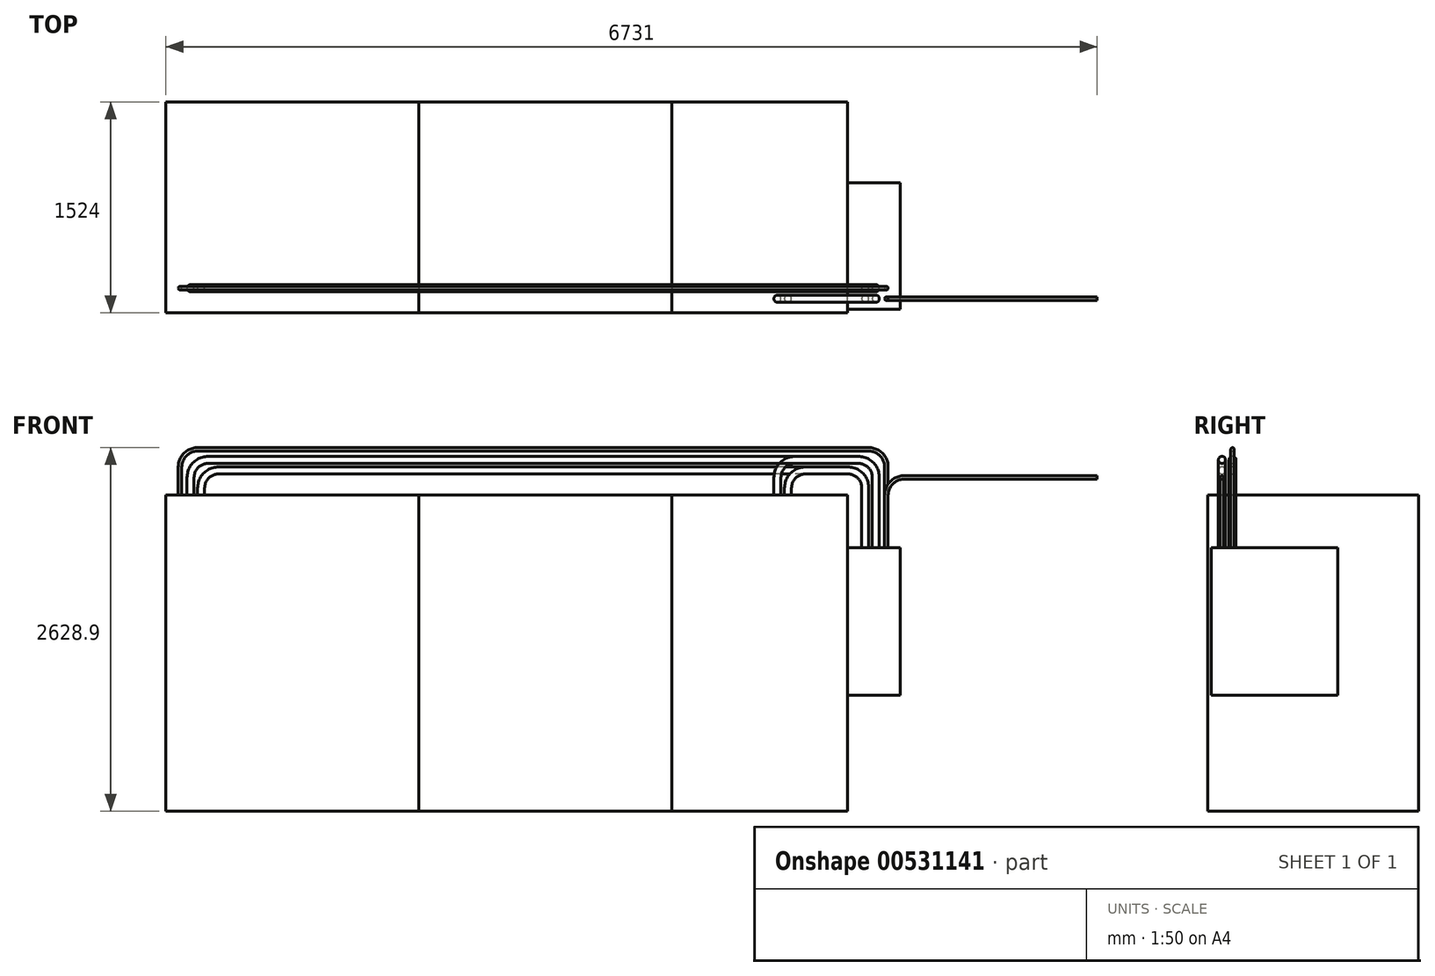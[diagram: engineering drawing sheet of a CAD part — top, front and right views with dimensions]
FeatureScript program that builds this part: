
annotation { "Feature Type Name" : "Feature", "Feature Type Description" : "" }
export const myFeature = defineFeature(function(context is Context, id is Id, definition is map)
    precondition{}
    {
        {
            var Q0;
            Q0=qCreatedBy(makeId("Top.planeOp"),FACE);
            var sketch = newSketch(context, id + "F0", { "sketchPlane" : qUnion([Q0])});
            skLineSegment(sketch, "E0.bottom", {"start": v(1828.8, 1524) * mm, "end": v(0, 1524) * mm});
            skLineSegment(sketch, "E0.top", {"start": v(1828.8, 0) * mm, "end": v(0, 0) * mm});
            skLineSegment(sketch, "E0.left", {"start": v(1828.8, 1524) * mm, "end": v(1828.8, 0) * mm});
            skLineSegment(sketch, "E0.right", {"start": v(0, 1524) * mm, "end": v(0, 0) * mm});
            skPoint(sketch, "E1.firstSnap0", {"position": v(0, 762) * mm});
            skPoint(sketch, "E2", {"position": v(0, 0) * mm});
            skSolve(sketch);
        }
        {
            var Q0;
            Q0=qCreatedBy(makeId("Top.planeOp"),FACE);
            var sketch = newSketch(context, id + "F1", { "sketchPlane" : qUnion([Q0])});
            skLineSegment(sketch, "E3.bottom", {"start": v(0, 0) * mm, "end": v(-1828.8, 0) * mm});
            skLineSegment(sketch, "E3.top", {"start": v(0, 1524) * mm, "end": v(-1828.8, 1524) * mm});
            skLineSegment(sketch, "E3.left", {"start": v(0, 0) * mm, "end": v(0, 1524) * mm});
            skLineSegment(sketch, "E3.right", {"start": v(-1828.8, 0) * mm, "end": v(-1828.8, 1524) * mm});
            skLineSegment(sketch, "E4.bottom", {"start": v(1828.8, 0) * mm, "end": v(3098.8, 0) * mm});
            skLineSegment(sketch, "E4.top", {"start": v(1828.8, 1524) * mm, "end": v(3098.8, 1524) * mm});
            skLineSegment(sketch, "E4.left", {"start": v(1828.8, 0) * mm, "end": v(1828.8, 1524) * mm});
            skLineSegment(sketch, "E4.right", {"start": v(3098.8, 0) * mm, "end": v(3098.8, 1524) * mm});
            skSolve(sketch);
        }
        {
            var Q0;
            Q0 = qSketchRegion(id + "F0", true);
            var Q1;
            Q1 = qSketchRegion(id + "F1", true);
            extrude(context, id + "F2", {"entities" : qUnion([Q0, Q1]), "depth" : 2286 * mm, "offsetDistance" : 25.4 * mm});
        }
        {
            var Q0;
            Q0=makeQuery(id+"F2.opExtrude","SWEPT_FACE",FACE,{"disambiguationData":[OSD([sQuery(id+"F1.wireOp",EDGE,"E4.right")])]});
            var sketch = newSketch(context, id + "F3", { "sketchPlane" : qUnion([Q0])});
            skLineSegment(sketch, "E5.bottom", {"start": v(25.4, 1905) * mm, "end": v(939.8, 1905) * mm});
            skLineSegment(sketch, "E5.top", {"start": v(25.4, 838.2) * mm, "end": v(939.8, 838.2) * mm});
            skLineSegment(sketch, "E5.left", {"start": v(25.4, 1905) * mm, "end": v(25.4, 838.2) * mm});
            skLineSegment(sketch, "E5.right", {"start": v(939.8, 1905) * mm, "end": v(939.8, 838.2) * mm});
            skSolve(sketch);
        }
        {
            var Q0;
            Q0 = qSketchRegion(id + "F3", true);
            extrude(context, id + "F4", {"entities" : qUnion([Q0]), "depth" : 381 * mm, "offsetDistance" : 25.4 * mm});
        }
        {
            var Q0;
            Q0=makeQuery(id+"F2.opExtrude","SWEPT_FACE",FACE,{"disambiguationData":[OSD([sQuery(id+"F1.wireOp",EDGE,"E4.bottom")])]});
            cPlane(context, id + "F5", {"entities" : qUnion([Q0]), "cplaneType" : CPlaneType.OFFSET, "offset" : 101.6 * mm, "oppositeDirection" : true, "width" : 152.4 * mm, "height" : 152.4 * mm});
        }
        {
            var Q0;
            Q0=qCreatedBy(id+"F5.planeOp",FACE);
            var sketch = newSketch(context, id + "F6", { "sketchPlane" : qUnion([Q0])});
            skLineSegment(sketch, "E6", {"start": v(3302, 1905) * mm, "end": v(3302, 2413) * mm});
            skLineSegment(sketch, "E7", {"start": v(3175, 2540) * mm, "end": v(2717.8, 2540) * mm});
            skLineSegment(sketch, "E8", {"start": v(2590.8, 2413) * mm, "end": v(2590.8, 2286) * mm});
            skPoint(sketch, "E9.visualSharp", {"position": v(2590.8, 2540) * mm});
            skArc(sketch, "E9.filletArc", {"start": v(2717.8, 2540) * mm, "mid": v(2628, 2502.8) * mm, "end": v(2590.8, 2413) * mm});
            skPoint(sketch, "E10.visualSharp", {"position": v(3302, 2540) * mm});
            skArc(sketch, "E10.filletArc", {"start": v(3302, 2413) * mm, "mid": v(3264.8, 2502.8) * mm, "end": v(3175, 2540) * mm});
            skLineSegment(sketch, "E11", {"start": v(3225.8, 1905) * mm, "end": v(3225.8, 2336.8) * mm});
            skLineSegment(sketch, "E12", {"start": v(3098.8, 2463.8) * mm, "end": v(2794, 2463.8) * mm});
            skLineSegment(sketch, "E13", {"start": v(2667, 2336.8) * mm, "end": v(2667, 2286) * mm});
            skPoint(sketch, "E14.visualSharp", {"position": v(2667, 2463.8) * mm});
            skArc(sketch, "E14.filletArc", {"start": v(2794, 2463.8) * mm, "mid": v(2704.2, 2426.6) * mm, "end": v(2667, 2336.8) * mm});
            skPoint(sketch, "E15.visualSharp", {"position": v(3225.8, 2463.8) * mm});
            skArc(sketch, "E15.filletArc", {"start": v(3225.8, 2336.8) * mm, "mid": v(3188.6, 2426.6) * mm, "end": v(3098.8, 2463.8) * mm});
            skLineSegment(sketch, "E16", {"start": v(3378.2, 1905) * mm, "end": v(3378.2, 2286) * mm});
            skLineSegment(sketch, "E17", {"start": v(3505.2, 2413) * mm, "end": v(4902.2, 2413) * mm});
            skPoint(sketch, "E18.visualSharp", {"position": v(3378.2, 2413) * mm});
            skArc(sketch, "E18.filletArc", {"start": v(3505.2, 2413) * mm, "mid": v(3415.4, 2375.8) * mm, "end": v(3378.2, 2286) * mm});
            skSolve(sketch);
        }
        {
            var Q0;
            Q0=makeQuery(id+"F4.opExtrude","SWEPT_FACE",FACE,{"disambiguationData":[OSD([sQuery(id+"F3.wireOp",EDGE,"E5.bottom")])]});
            var sketch = newSketch(context, id + "F7", { "sketchPlane" : qUnion([Q0])});
            skCircle(sketch, "E19", {"center": v(3302, 101.6) * mm, "radius": 25.4 * mm});
            skCircle(sketch, "E20", {"center": v(3225.8, 101.6) * mm, "radius": 25.4 * mm});
            skCircle(sketch, "E21", {"center": v(3378.2, 101.6) * mm, "radius": 12.7 * mm});
            skSolve(sketch);
        }
        {
            var Q0;
            Q0=makeQuery(id+"F7.imprint","IMPRINT",FACE,{"disambiguationData":[TD([[makeQuery(id+"F7.imprint","IMPRINT",EDGE,{"derivedFrom":sQuery(id+"F7.wireOp",EDGE,"E19")}),1.0]])]});
            var Q1;
            Q1=sQuery(id+"F6.wireOp",EDGE,"E6");
            var Q2;
            Q2=sQuery(id+"F6.wireOp",EDGE,"E10.filletArc");
            var Q3;
            Q3=sQuery(id+"F6.wireOp",EDGE,"E7");
            var Q4;
            Q4=sQuery(id+"F6.wireOp",EDGE,"E9.filletArc");
            var Q5;
            Q5=sQuery(id+"F6.wireOp",EDGE,"E8");
            sweep(context, id + "F8", {"profiles" : qUnion([Q0]), "path" : qUnion([Q1, Q2, Q3, Q4, Q5])});
        }
        {
            var Q0;
            Q0=makeQuery(id+"F7.imprint","IMPRINT",FACE,{"disambiguationData":[TD([[makeQuery(id+"F7.imprint","IMPRINT",EDGE,{"derivedFrom":sQuery(id+"F7.wireOp",EDGE,"E20")}),1.0]])]});
            var Q1;
            Q1=sQuery(id+"F6.wireOp",EDGE,"E11");
            var Q2;
            Q2=sQuery(id+"F6.wireOp",EDGE,"E15.filletArc");
            var Q3;
            Q3=sQuery(id+"F6.wireOp",EDGE,"E12");
            var Q4;
            Q4=sQuery(id+"F6.wireOp",EDGE,"E14.filletArc");
            var Q5;
            Q5=sQuery(id+"F6.wireOp",EDGE,"E13");
            sweep(context, id + "F9", {"profiles" : qUnion([Q0]), "path" : qUnion([Q1, Q2, Q3, Q4, Q5])});
        }
        {
            var Q0;
            Q0=makeQuery(id+"F7.imprint","IMPRINT",FACE,{"disambiguationData":[TD([[makeQuery(id+"F7.imprint","IMPRINT",EDGE,{"derivedFrom":sQuery(id+"F7.wireOp",EDGE,"E21")}),1.0]])]});
            var Q1;
            Q1=sQuery(id+"F6.wireOp",EDGE,"E16");
            var Q2;
            Q2=sQuery(id+"F6.wireOp",EDGE,"E18.filletArc");
            var Q3;
            Q3=sQuery(id+"F6.wireOp",EDGE,"E17");
            sweep(context, id + "F10", {"profiles" : qUnion([Q0]), "path" : qUnion([Q1, Q2, Q3])});
        }
        {
            var Q0;
            Q0=makeQuery(id+"F2.opExtrude","SWEPT_FACE",FACE,{"disambiguationData":[OSD([sQuery(id+"F1.wireOp",EDGE,"E4.bottom")])]});
            cPlane(context, id + "F11", {"entities" : qUnion([Q0]), "cplaneType" : CPlaneType.OFFSET, "offset" : 177.8 * mm, "oppositeDirection" : true, "width" : 152.4 * mm, "height" : 152.4 * mm});
        }
        {
            var Q0;
            Q0=qCreatedBy(id+"F11.planeOp",FACE);
            var sketch = newSketch(context, id + "F12", { "sketchPlane" : qUnion([Q0])});
            skLineSegment(sketch, "E22", {"start": v(3378.2, 1905) * mm, "end": v(3378.2, 2489.2) * mm});
            skLineSegment(sketch, "E23", {"start": v(3251.2, 2616.2) * mm, "end": v(-1600.2, 2616.2) * mm});
            skLineSegment(sketch, "E24", {"start": v(-1727.2, 2489.2) * mm, "end": v(-1727.2, 2286) * mm});
            skPoint(sketch, "E25.visualSharp", {"position": v(-1727.2, 2616.2) * mm});
            skArc(sketch, "E25.filletArc", {"start": v(-1600.2, 2616.2) * mm, "mid": v(-1690, 2579) * mm, "end": v(-1727.2, 2489.2) * mm});
            skPoint(sketch, "E26.visualSharp", {"position": v(3378.2, 2616.2) * mm});
            skArc(sketch, "E26.filletArc", {"start": v(3378.2, 2489.2) * mm, "mid": v(3341, 2579) * mm, "end": v(3251.2, 2616.2) * mm});
            skLineSegment(sketch, "E27", {"start": v(3302, 1905) * mm, "end": v(3302, 2413) * mm});
            skLineSegment(sketch, "E28", {"start": v(3175, 2540) * mm, "end": v(-1524, 2540) * mm});
            skLineSegment(sketch, "E29", {"start": v(-1651, 2413) * mm, "end": v(-1651, 2286) * mm});
            skPoint(sketch, "E30.visualSharp", {"position": v(-1651, 2540) * mm});
            skArc(sketch, "E30.filletArc", {"start": v(-1524, 2540) * mm, "mid": v(-1613.8, 2502.8) * mm, "end": v(-1651, 2413) * mm});
            skPoint(sketch, "E31.visualSharp", {"position": v(3302, 2540) * mm});
            skArc(sketch, "E31.filletArc", {"start": v(3302, 2413) * mm, "mid": v(3264.8, 2502.8) * mm, "end": v(3175, 2540) * mm});
            skLineSegment(sketch, "E32", {"start": v(3225.8, 1905) * mm, "end": v(3225.8, 2336.8) * mm});
            skLineSegment(sketch, "E33", {"start": v(3098.8, 2463.8) * mm, "end": v(-1447.8, 2463.8) * mm});
            skLineSegment(sketch, "E34", {"start": v(-1574.8, 2336.8) * mm, "end": v(-1574.8, 2286) * mm});
            skPoint(sketch, "E35.visualSharp", {"position": v(-1574.8, 2463.8) * mm});
            skArc(sketch, "E35.filletArc", {"start": v(-1447.8, 2463.8) * mm, "mid": v(-1537.6, 2426.6) * mm, "end": v(-1574.8, 2336.8) * mm});
            skPoint(sketch, "E36.visualSharp", {"position": v(3225.8, 2463.8) * mm});
            skArc(sketch, "E36.filletArc", {"start": v(3225.8, 2336.8) * mm, "mid": v(3188.6, 2426.6) * mm, "end": v(3098.8, 2463.8) * mm});
            skSolve(sketch);
        }
        {
            var Q0;
            Q0=makeQuery(id+"F4.opExtrude","SWEPT_FACE",FACE,{"disambiguationData":[OSD([sQuery(id+"F3.wireOp",EDGE,"E5.bottom")])]});
            var sketch = newSketch(context, id + "F13", { "sketchPlane" : qUnion([Q0])});
            skCircle(sketch, "E37", {"center": v(3378.2, 177.8) * mm, "radius": 12.7 * mm});
            skCircle(sketch, "E38", {"center": v(3302, 177.8) * mm, "radius": 25.4 * mm});
            skCircle(sketch, "E39", {"center": v(3225.8, 177.8) * mm, "radius": 25.4 * mm});
            skSolve(sketch);
        }
        {
            var Q0;
            Q0=makeQuery(id+"F13.imprint","IMPRINT",FACE,{"disambiguationData":[TD([[makeQuery(id+"F13.imprint","IMPRINT",EDGE,{"derivedFrom":sQuery(id+"F13.wireOp",EDGE,"E38")}),1.0]])]});
            var Q1;
            Q1=sQuery(id+"F12.wireOp",EDGE,"E27");
            var Q2;
            Q2=sQuery(id+"F12.wireOp",EDGE,"E31.filletArc");
            var Q3;
            Q3=sQuery(id+"F12.wireOp",EDGE,"E28");
            var Q4;
            Q4=sQuery(id+"F12.wireOp",EDGE,"E30.filletArc");
            var Q5;
            Q5=sQuery(id+"F12.wireOp",EDGE,"E29");
            sweep(context, id + "F14", {"profiles" : qUnion([Q0]), "path" : qUnion([Q1, Q2, Q3, Q4, Q5])});
        }
        {
            var Q0;
            Q0=makeQuery(id+"F13.imprint","IMPRINT",FACE,{"disambiguationData":[TD([[makeQuery(id+"F13.imprint","IMPRINT",EDGE,{"derivedFrom":sQuery(id+"F13.wireOp",EDGE,"E37")}),1.0]])]});
            var Q1;
            Q1=sQuery(id+"F12.wireOp",EDGE,"E24");
            var Q2;
            Q2=sQuery(id+"F12.wireOp",EDGE,"E25.filletArc");
            var Q3;
            Q3=sQuery(id+"F12.wireOp",EDGE,"E23");
            var Q4;
            Q4=sQuery(id+"F12.wireOp",EDGE,"E26.filletArc");
            var Q5;
            Q5=sQuery(id+"F12.wireOp",EDGE,"E22");
            sweep(context, id + "F15", {"profiles" : qUnion([Q0]), "path" : qUnion([Q1, Q2, Q3, Q4, Q5])});
        }
        {
            var Q0;
            Q0=makeQuery(id+"F13.imprint","IMPRINT",FACE,{"disambiguationData":[TD([[makeQuery(id+"F13.imprint","IMPRINT",EDGE,{"derivedFrom":sQuery(id+"F13.wireOp",EDGE,"E39")}),1.0]])]});
            var Q1;
            Q1=sQuery(id+"F12.wireOp",EDGE,"E32");
            var Q2;
            Q2=sQuery(id+"F12.wireOp",EDGE,"E36.filletArc");
            var Q3;
            Q3=sQuery(id+"F12.wireOp",EDGE,"E33");
            var Q4;
            Q4=sQuery(id+"F12.wireOp",EDGE,"E35.filletArc");
            var Q5;
            Q5=sQuery(id+"F12.wireOp",EDGE,"E34");
            sweep(context, id + "F16", {"profiles" : qUnion([Q0]), "path" : qUnion([Q1, Q2, Q3, Q4, Q5])});
        }
    });
